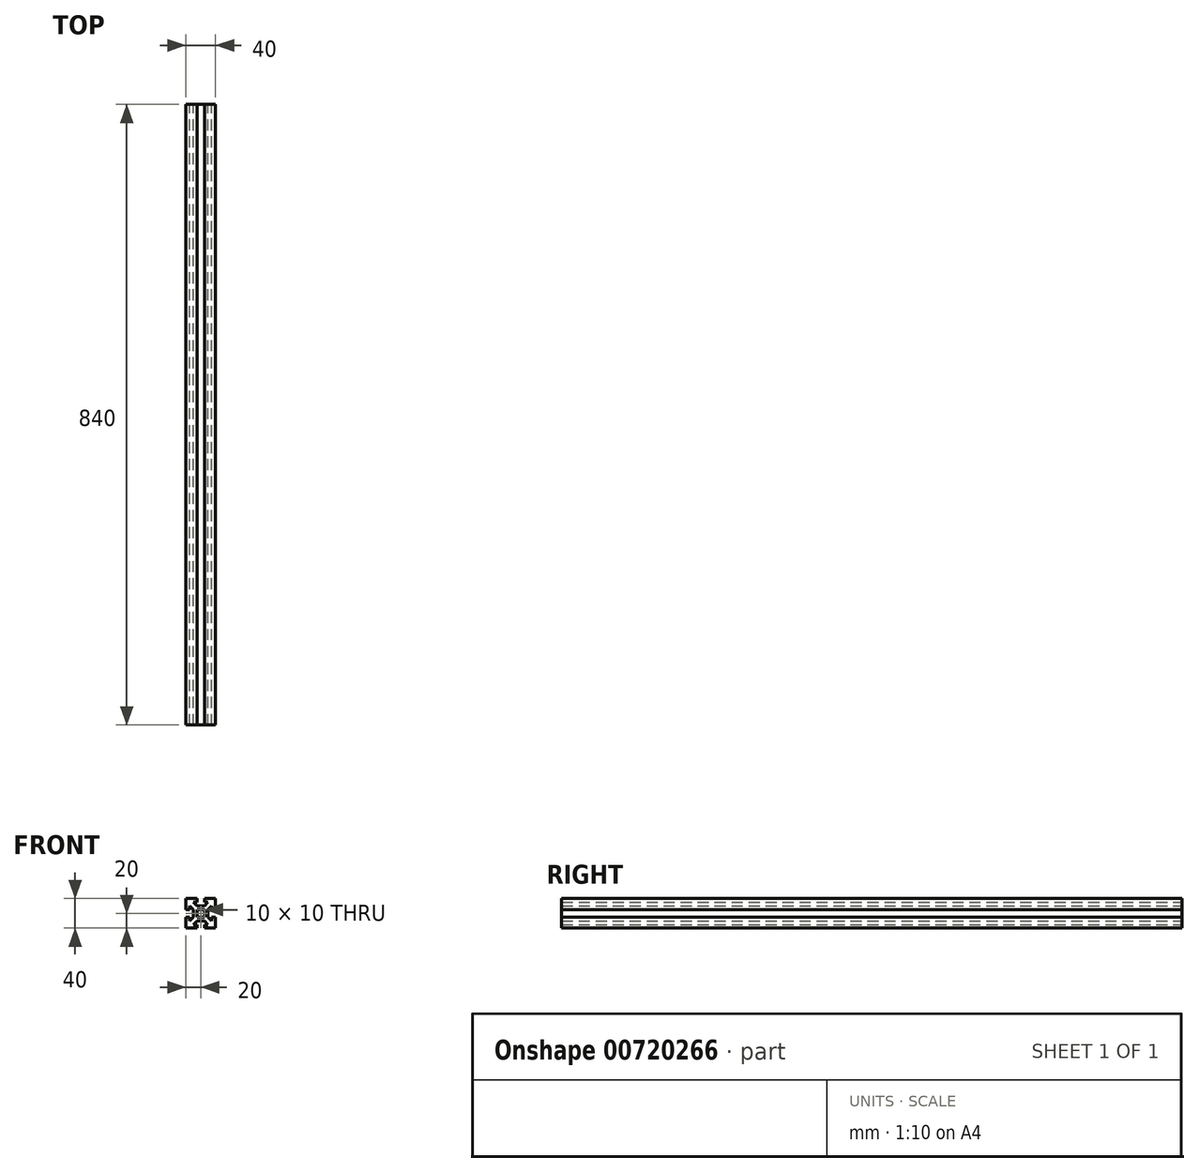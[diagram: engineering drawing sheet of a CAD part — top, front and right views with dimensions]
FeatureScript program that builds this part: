
annotation { "Feature Type Name" : "Feature", "Feature Type Description" : "" }
export const myFeature = defineFeature(function(context is Context, id is Id, definition is map)
    precondition{}
    {
        {
            var Q0;
            Q0=qCreatedBy(makeId("Front.planeOp"),FACE);
            var sketch = newSketch(context, id + "F0", { "sketchPlane" : qUnion([Q0])});
            skLineSegment(sketch, "E0.bottom", {"start": v(20, 20) * mm, "end": v(5, 20) * mm});
            skLineSegment(sketch, "E0.top", {"start": v(20, -20) * mm, "end": v(5, -20) * mm});
            skLineSegment(sketch, "E0.left", {"start": v(20, 20) * mm, "end": v(20, 5) * mm});
            skLineSegment(sketch, "E0.right", {"start": v(-20, 20) * mm, "end": v(-20, 5) * mm});
            skPoint(sketch, "E0.middle", {"position": v(0, 0) * mm});
            skLineSegment(sketch, "E1", {"start": v(0, 20) * mm, "end": v(0, -20) * mm, "construction": true});
            skLineSegment(sketch, "E2", {"start": v(-20, 0) * mm, "end": v(20, 0) * mm, "construction": true});
            skLineSegment(sketch, "E3", {"start": v(-20, 5) * mm, "end": v(-15, 5) * mm});
            skLineSegment(sketch, "E4", {"start": v(-20, -5) * mm, "end": v(-15, -5) * mm});
            skLineSegment(sketch, "E5", {"start": v(-5, 20) * mm, "end": v(-5, 15) * mm});
            skLineSegment(sketch, "E6", {"start": v(5, 20) * mm, "end": v(5, 15) * mm});
            skLineSegment(sketch, "E7", {"start": v(-10, 15) * mm, "end": v(-5, 15) * mm});
            skLineSegment(sketch, "E8", {"start": v(-10, -15) * mm, "end": v(-5, -15) * mm});
            skLineSegment(sketch, "E9", {"start": v(15, 10) * mm, "end": v(15, 5) * mm});
            skLineSegment(sketch, "E10", {"start": v(-15, 10) * mm, "end": v(-10, 5) * mm});
            skLineSegment(sketch, "E11", {"start": v(-10, 15) * mm, "end": v(-5, 10) * mm});
            skLineSegment(sketch, "E12", {"start": v(-15, -10) * mm, "end": v(-10, -5) * mm});
            skLineSegment(sketch, "E13", {"start": v(-10, -15) * mm, "end": v(-5, -10) * mm});
            skLineSegment(sketch, "E14.trimOffspring", {"start": v(20, -5) * mm, "end": v(20, -20) * mm});
            skLineSegment(sketch, "E15.trimOffspring", {"start": v(-20, -5) * mm, "end": v(-20, -20) * mm});
            skLineSegment(sketch, "E16.trimOffspring", {"start": v(-5, -20) * mm, "end": v(-20, -20) * mm});
            skLineSegment(sketch, "E17.trimOffspring", {"start": v(-5, 20) * mm, "end": v(-20, 20) * mm});
            skLineSegment(sketch, "E18.trimOffspring", {"start": v(5, 15) * mm, "end": v(10, 15) * mm});
            skLineSegment(sketch, "E19.trimOffspring", {"start": v(-15, -5) * mm, "end": v(-15, -10) * mm});
            skLineSegment(sketch, "E20.trimOffspring", {"start": v(15, -5) * mm, "end": v(15, -10) * mm});
            skLineSegment(sketch, "E21.trimOffspring", {"start": v(5, -15) * mm, "end": v(10, -15) * mm});
            skLineSegment(sketch, "E22.trimOffspring", {"start": v(-5, 5) * mm, "end": v(-5, -5) * mm});
            skLineSegment(sketch, "E23.trimOffspring", {"start": v(5, 5) * mm, "end": v(5, -5) * mm});
            skLineSegment(sketch, "E24.trimOffspring", {"start": v(15, 5) * mm, "end": v(20, 5) * mm});
            skLineSegment(sketch, "E25.trimOffspring", {"start": v(15, -5) * mm, "end": v(20, -5) * mm});
            skLineSegment(sketch, "E26.trimOffspring", {"start": v(5, -15) * mm, "end": v(5, -20) * mm});
            skLineSegment(sketch, "E27.trimOffspring", {"start": v(-5, -15) * mm, "end": v(-5, -20) * mm});
            skLineSegment(sketch, "E28.trimOffspring", {"start": v(-5, -5) * mm, "end": v(5, -5) * mm});
            skLineSegment(sketch, "E29.trimOffspring", {"start": v(-5, 5) * mm, "end": v(5, 5) * mm});
            skLineSegment(sketch, "E30", {"start": v(10, 5) * mm, "end": v(10, -5) * mm});
            skLineSegment(sketch, "E31", {"start": v(-5, 10) * mm, "end": v(5, 10) * mm});
            skLineSegment(sketch, "E32", {"start": v(-10, 5) * mm, "end": v(-10, -5) * mm});
            skLineSegment(sketch, "E33", {"start": v(-5, -10) * mm, "end": v(5, -10) * mm});
            skLineSegment(sketch, "E34.trimOffspring", {"start": v(-15, 10) * mm, "end": v(-15, 5) * mm});
            skPoint(sketch, "E35.orphan", {"position": v(20, 15) * mm});
            skPoint(sketch, "E36.orphan", {"position": v(20, -15) * mm});
            skPoint(sketch, "E37.orphan", {"position": v(15, -20) * mm});
            skPoint(sketch, "E38.orphan", {"position": v(-15, -20) * mm});
            skLineSegment(sketch, "E39.trimOffspring", {"start": v(-5, 0) * mm, "end": v(0, -5) * mm});
            skLineSegment(sketch, "E40.trimOffspring", {"start": v(-5, 0) * mm, "end": v(0, 5) * mm});
            skLineSegment(sketch, "E41.trimOffspring", {"start": v(0, 5) * mm, "end": v(5, 0) * mm});
            skLineSegment(sketch, "E42.trimOffspring", {"start": v(5, 10) * mm, "end": v(10, 15) * mm});
            skLineSegment(sketch, "E43.trimOffspring", {"start": v(10, 5) * mm, "end": v(15, 10) * mm});
            skLineSegment(sketch, "E44.trimOffspring", {"start": v(10, -5) * mm, "end": v(15, -10) * mm});
            skLineSegment(sketch, "E45.trimOffspring", {"start": v(5, -10) * mm, "end": v(10, -15) * mm});
            skLineSegment(sketch, "E46.trimOffspring", {"start": v(0, -5) * mm, "end": v(5, 0) * mm});
            skSolve(sketch);
        }
        {
            var Q0;
            Q0=makeQuery(id+"F0.imprint","IMPRINT",FACE,{"disambiguationData":[TD([[makeQuery(id+"F0.imprint","IMPRINT",EDGE,{"derivedFrom":sQuery(id+"F0.wireOp",EDGE,"E0.bottom")}),1.0]])]});
            extrude(context, id + "F1", {"entities" : qUnion([Q0]), "depth" : 840 * mm, "offsetDistance" : 25 * mm});
        }
    });
